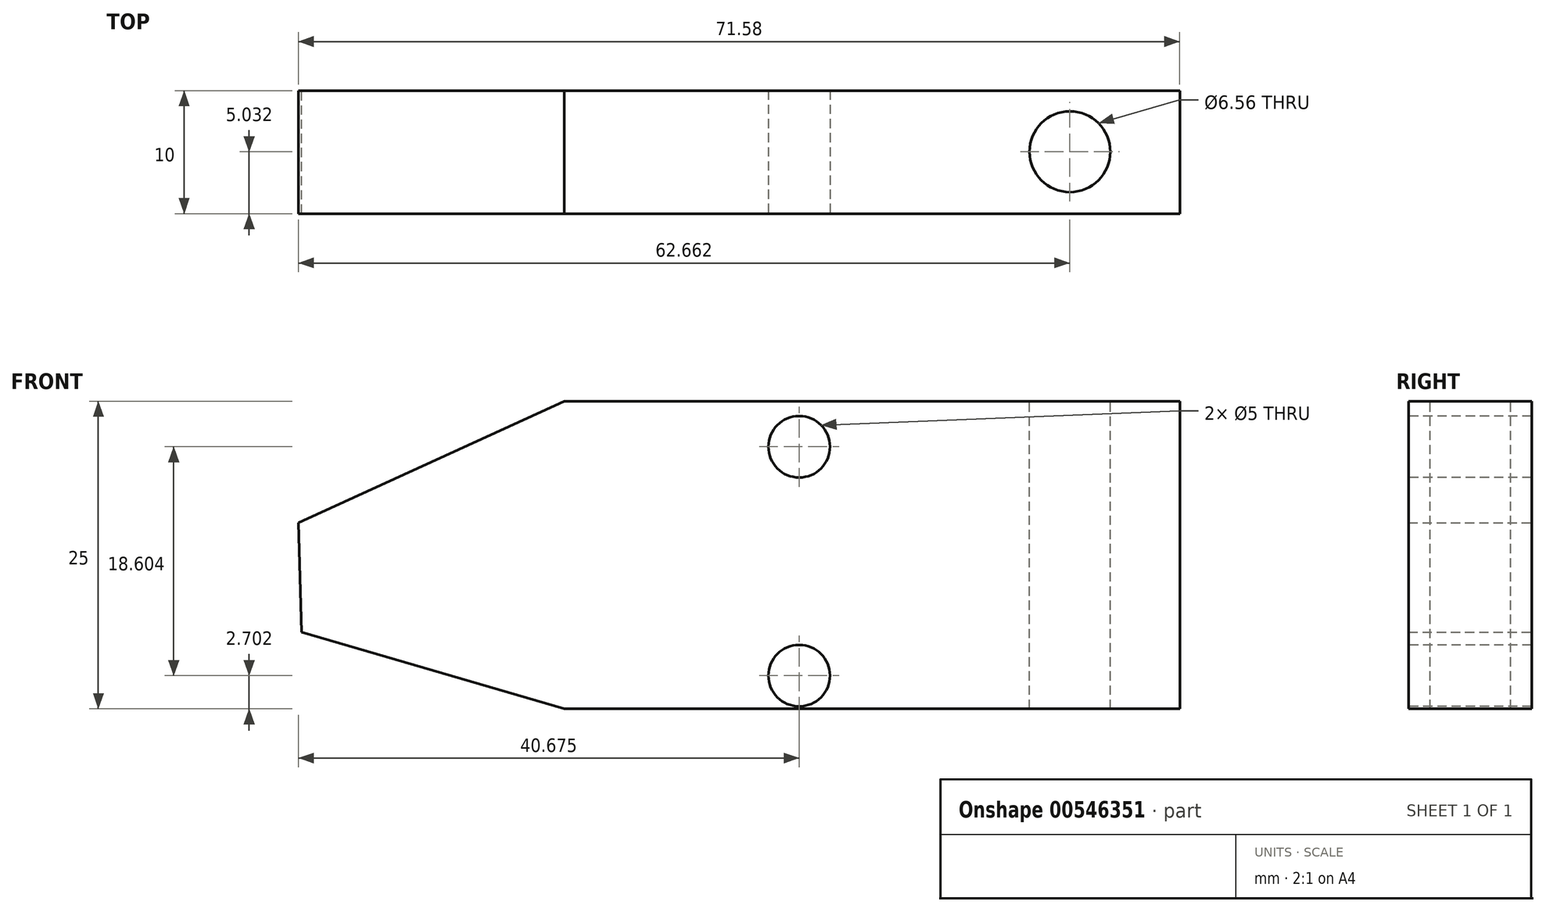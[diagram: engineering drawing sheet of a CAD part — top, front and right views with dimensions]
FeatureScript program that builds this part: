
annotation { "Feature Type Name" : "Feature", "Feature Type Description" : "" }
export const myFeature = defineFeature(function(context is Context, id is Id, definition is map)
    precondition{}
    {
        {
            var Q0;
            Q0=qCreatedBy(makeId("Front.planeOp"),FACE);
            var sketch = newSketch(context, id + "F0", { "sketchPlane" : qUnion([Q0])});
            skLineSegment(sketch, "E0.bottom", {"start": v(-11.59, 12.9) * mm, "end": v(13.41, 12.9) * mm});
            skLineSegment(sketch, "E0.top", {"start": v(-11.59, -12.1) * mm, "end": v(13.41, -12.1) * mm});
            skLineSegment(sketch, "E0.left", {"start": v(-11.59, 12.9) * mm, "end": v(-11.59, -12.1) * mm});
            skLineSegment(sketch, "E0.right", {"start": v(13.41, 12.9) * mm, "end": v(13.41, -12.1) * mm});
            skLineSegment(sketch, "E1", {"start": v(-11.59, 12.9) * mm, "end": v(-33.17, 3) * mm});
            skLineSegment(sketch, "E2", {"start": v(-11.59, -12.1) * mm, "end": v(-32.91, -5.88) * mm});
            skLineSegment(sketch, "E3", {"start": v(-33.17, 3) * mm, "end": v(-32.91, -5.88) * mm});
            skSolve(sketch);
        }
        {
            var Q0;
            Q0=makeQuery(id+"F0.imprint","IMPRINT",FACE,{"disambiguationData":[TD([[makeQuery(id+"F0.imprint","IMPRINT",EDGE,{"derivedFrom":sQuery(id+"F0.wireOp",EDGE,"E0.left")}),-1.0]])]});
            var Q1;
            Q1=makeQuery(id+"F0.imprint","IMPRINT",FACE,{"disambiguationData":[TD([[makeQuery(id+"F0.imprint","IMPRINT",EDGE,{"derivedFrom":sQuery(id+"F0.wireOp",EDGE,"E0.bottom")}),-1.0]])]});
            extrude(context, id + "F1", {"entities" : qUnion([Q0, Q1]), "depth" : 10 * mm, "offsetDistance" : 25 * mm});
        }
        {
            var Q0;
            Q0=makeQuery(id+"F1.opExtrude","CAP_FACE",FACE,{"disambiguationData":[OSD([sQuery(id+"F0.wireOp",EDGE,"E0.bottom"),sQuery(id+"F0.wireOp",EDGE,"E0.top"),sQuery(id+"F0.wireOp",EDGE,"E0.right"),sQuery(id+"F0.wireOp",EDGE,"E1"),sQuery(id+"F0.wireOp",EDGE,"E2"),sQuery(id+"F0.wireOp",EDGE,"E3")])],"isStart":false});
            var sketch = newSketch(context, id + "F2", { "sketchPlane" : qUnion([Q0])});
            skCircle(sketch, "E4", {"center": v(7.5, 9.2) * mm, "radius": 2.84 * mm});
            skCircle(sketch, "E5", {"center": v(7.5, -9.4) * mm, "radius": 2.7 * mm});
            skSolve(sketch);
        }
        {
            var Q0;
            Q0=sQuery(id+"F2.wireOp",VERTEX,"E4.center");
            var Q1;
            Q1=sQuery(id+"F2.wireOp",VERTEX,"E5.center");
            var Q2;
            Q2=makeQuery(id+"F1.opExtrude","SWEPT_BODY",BODY,{"disambiguationData":[OSD([sQuery(id+"F0.wireOp",EDGE,"E0.bottom"),sQuery(id+"F0.wireOp",EDGE,"E0.top"),sQuery(id+"F0.wireOp",EDGE,"E0.right"),sQuery(id+"F0.wireOp",EDGE,"E1"),sQuery(id+"F0.wireOp",EDGE,"E2"),sQuery(id+"F0.wireOp",EDGE,"E3")])]});
            hole(context, id + "F3", {"style" : HoleStyle.SIMPLE, "endStyle" : HoleEndStyle.THROUGH, "holeDiameter" : 5 * mm, "isTappedThrough" : true, "tappedDepth" : 12 * mm, "tapClearance" : 3, "locations" : qUnion([Q0, Q1]), "scope" : qUnion([Q2])});
        }
        {
            var Q0;
            Q0=makeQuery(id+"F1.opExtrude","SWEPT_FACE",FACE,{"disambiguationData":[OSD([sQuery(id+"F0.wireOp",EDGE,"E0.right")])]});
            var sketch = newSketch(context, id + "F4", { "sketchPlane" : qUnion([Q0])});
            skLineSegment(sketch, "E6.bottom", {"start": v(-10, 12.9) * mm, "end": v(0, 12.9) * mm});
            skLineSegment(sketch, "E6.top", {"start": v(-10, -12.1) * mm, "end": v(0, -12.1) * mm});
            skLineSegment(sketch, "E6.left", {"start": v(-10, 12.9) * mm, "end": v(-10, -12.1) * mm});
            skLineSegment(sketch, "E6.right", {"start": v(0, 12.9) * mm, "end": v(0, -12.1) * mm});
            skSolve(sketch);
        }
        {
            var Q0;
            Q0 = qSketchRegion(id + "F4", true);
            extrude(context, id + "F5", {"entities" : qUnion([Q0]), "operationType" : NewBodyOperationType.ADD, "depth" : 25 * mm, "offsetDistance" : 25 * mm});
        }
        {
            var Q0;
            Q0=makeQuery(id+"F5.boolean.opBoolean","MERGE",FACE,{"derivedFrom":[makeQuery(id+"F1.opExtrude","SWEPT_FACE",FACE,{"disambiguationData":[OSD([sQuery(id+"F0.wireOp",EDGE,"E0.bottom")])]}),makeQuery(id+"F5.opExtrude","SWEPT_FACE",FACE,{"disambiguationData":[OSD([sQuery(id+"F4.wireOp",EDGE,"E6.bottom")])]})]});
            var sketch = newSketch(context, id + "F6", { "sketchPlane" : qUnion([Q0])});
            skCircle(sketch, "E7", {"center": v(29.5, -4.97) * mm, "radius": 3.28 * mm});
            skSolve(sketch);
        }
        {
            var Q0;
            Q0 = qSketchRegion(id + "F6", true);
            extrude(context, id + "F7", {"entities" : qUnion([Q0]), "operationType" : NewBodyOperationType.REMOVE, "oppositeDirection" : true, "depth" : 25 * mm, "offsetDistance" : 25 * mm});
        }
    });
